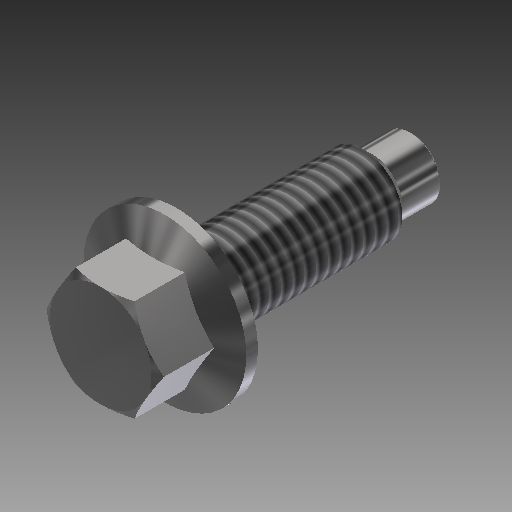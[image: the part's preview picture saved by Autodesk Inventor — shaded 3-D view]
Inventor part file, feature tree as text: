
AUTODESK INVENTOR PART (.ipt)
format: ipt  version: 2019 (Build 230136000, 136)  size: 204,288 bytes
history: native  units: mm
features: sketch x3, revolve x2, extrude x1, thread x1, fillet x1, projected_geometry x1
ambient origin geometry x8: Origin, YZ Plane, XZ Plane, XY Plane, X Axis, Y Axis, Z Axis, Center Point
bodies: Solid1 (feature_tree)
feature tree (9):
  extrude  "Extrusion1"  Depth=9.7mm TaperAngle=0.0deg
  revolve  "Revolution1"  [1 undecoded]
  revolve  "Revolution2"  [1 undecoded]
  thread  "Thread1"  [1 undecoded]
  fillet  "Fillet1"  Radius=30.0mm
  sketch  "Sketch1"  dims[d0=13.0mm d1=9.7mm d2=0.0mm]
  sketch  "Sketch2"  dims[d3=1.5mm d4=10.4mm]
  projected_geometry  "Projected Loop1"
  sketch  "Sketch3"  dims[d5=22.5deg d7=5.0mm d8=3.85mm d9=30.0mm d10=5.0mm d11=1.15mm d12=90.0deg d13=30.0deg d14=1.005553mm d16=6.5mm d17=90.0deg d18=10.0mm d19=0.0mm d20=0.2mm]
note: 3 required parameter values undecoded (feature->parameter linkage not recoverable at this tier; creation-order binding heuristic only, values carry confidence <= 0.55)